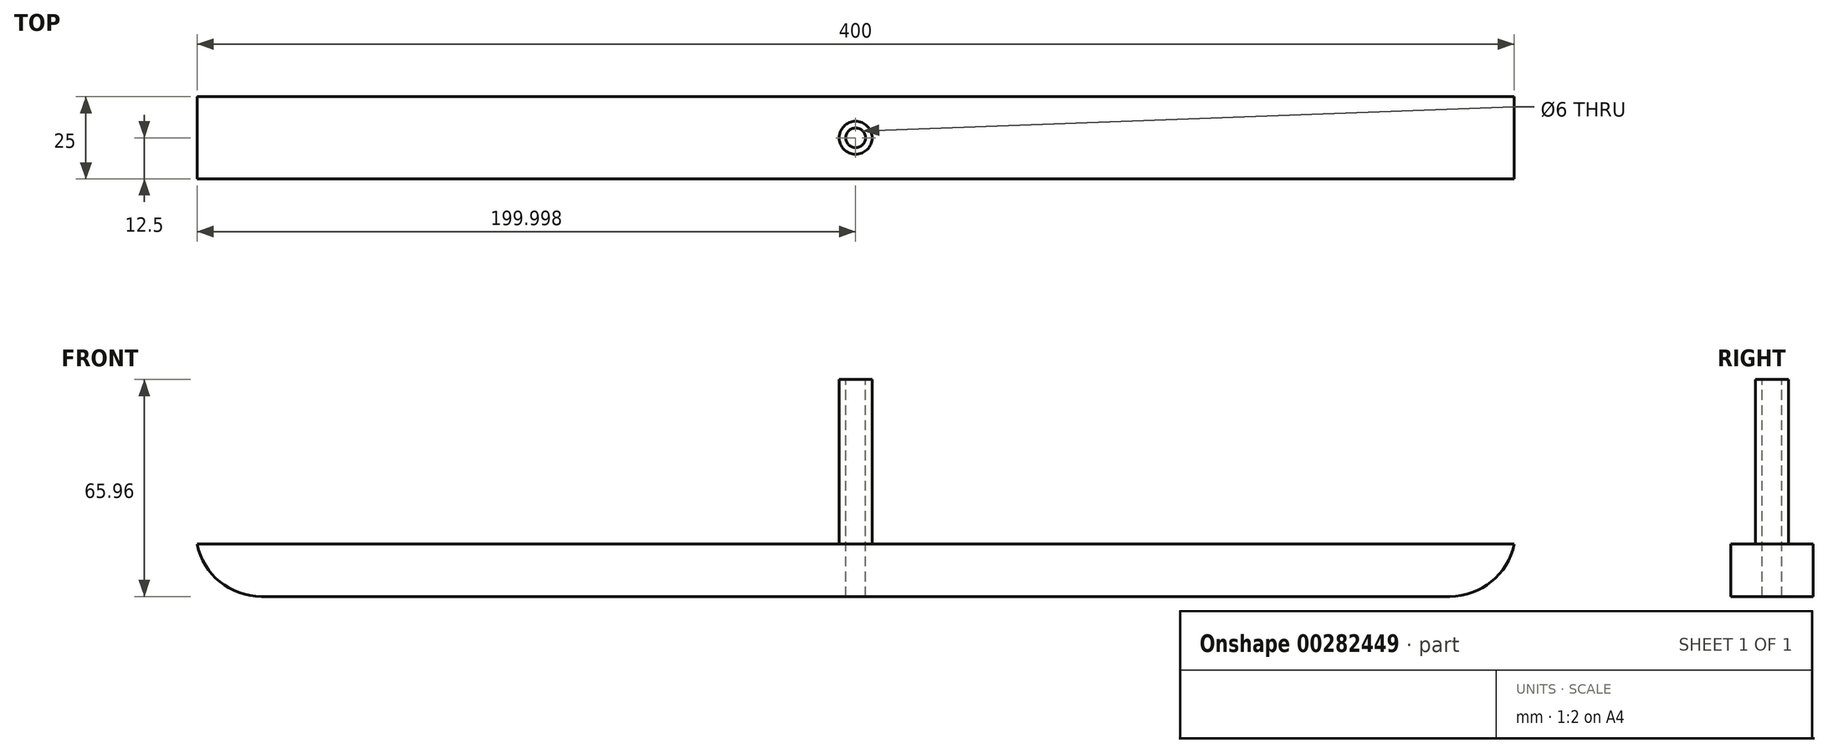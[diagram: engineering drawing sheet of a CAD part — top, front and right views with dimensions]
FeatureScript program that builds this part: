
annotation { "Feature Type Name" : "Feature", "Feature Type Description" : "" }
export const myFeature = defineFeature(function(context is Context, id is Id, definition is map)
    precondition{}
    {
        {
            var Q0;
            Q0=qCreatedBy(makeId("Front.planeOp"),FACE);
            var sketch = newSketch(context, id + "F0", { "sketchPlane" : qUnion([Q0])});
            skLineSegment(sketch, "E0.bottom", {"start": v(-70.22, 41.14) * mm, "end": v(329.78, 41.14) * mm});
            skLineSegment(sketch, "E0.top", {"start": v(-70.22, 25.18) * mm, "end": v(329.78, 25.18) * mm});
            skLineSegment(sketch, "E0.left", {"start": v(-70.22, 41.14) * mm, "end": v(-70.22, 25.18) * mm});
            skLineSegment(sketch, "E0.right", {"start": v(329.78, 41.14) * mm, "end": v(329.78, 25.18) * mm});
            skLineSegment(sketch, "E1.bottom", {"start": v(-70.22, 25.18) * mm, "end": v(-60.22, 25.18) * mm});
            skLineSegment(sketch, "E1.top", {"start": v(-70.22, -49.82) * mm, "end": v(-60.22, -49.82) * mm});
            skLineSegment(sketch, "E1.left", {"start": v(-70.22, 25.18) * mm, "end": v(-70.22, -49.82) * mm});
            skLineSegment(sketch, "E1.right", {"start": v(-60.22, 25.18) * mm, "end": v(-60.22, -49.82) * mm});
            skLineSegment(sketch, "E2.bottom", {"start": v(329.78, 25.18) * mm, "end": v(319.78, 25.18) * mm});
            skLineSegment(sketch, "E2.top", {"start": v(329.78, -49.82) * mm, "end": v(319.78, -49.82) * mm});
            skLineSegment(sketch, "E2.left", {"start": v(329.78, 25.18) * mm, "end": v(329.78, -49.82) * mm});
            skLineSegment(sketch, "E2.right", {"start": v(319.78, 25.18) * mm, "end": v(319.78, -49.82) * mm});
            skLineSegment(sketch, "E3", {"start": v(129.78, 25.18) * mm, "end": v(129.78, 66.56) * mm});
            skPoint(sketch, "E3.endSnap0", {"position": v(129.78, 41.14) * mm});
            skSolve(sketch);
        }
        {
            var Q0;
            Q0=makeQuery(id+"F0.imprint","IMPRINT",FACE,{"disambiguationData":[TD([[makeQuery(id+"F0.imprint","IMPRINT",EDGE,{"derivedFrom":sQuery(id+"F0.wireOp",EDGE,"E0.bottom")}),-1.0]])]});
            var Q1;
            Q1=makeQuery(id+"F0.imprint","IMPRINT",FACE,{"disambiguationData":[TD([[makeQuery(id+"F0.imprint","IMPRINT",EDGE,{"derivedFrom":sQuery(id+"F0.wireOp",EDGE,"E1.bottom")}),-1.0]])]});
            var Q2;
            Q2=makeQuery(id+"F0.imprint","IMPRINT",FACE,{"disambiguationData":[TD([[makeQuery(id+"F0.imprint","IMPRINT",EDGE,{"derivedFrom":sQuery(id+"F0.wireOp",EDGE,"E2.bottom")}),1.0]])]});
            extrude(context, id + "F1", {"entities" : qUnion([Q0, Q1, Q2]), "endBound" : BoundingType.SYMMETRIC, "depth" : 25 * mm});
        }
        {
            var Q0;
            Q0=makeQuery(id+"F1.opExtrude","SWEPT_FACE",FACE,{"disambiguationData":[OSD([sQuery(id+"F0.wireOp",EDGE,"E0.left"),sQuery(id+"F0.wireOp",EDGE,"E1.left")])]});
            var sketch = newSketch(context, id + "F2", { "sketchPlane" : qUnion([Q0])});
            skCircle(sketch, "E4", {"center": v(0, -29.82) * mm, "radius": 5 * mm});
            skSolve(sketch);
        }
        {
            var Q0;
            Q0=makeQuery(id+"F2.imprint","IMPRINT",FACE,{"disambiguationData":[TD([[makeQuery(id+"F2.imprint","IMPRINT",EDGE,{"derivedFrom":sQuery(id+"F2.wireOp",EDGE,"E4")}),1.0]])]});
            extrude(context, id + "F3", {"entities" : qUnion([Q0]), "operationType" : NewBodyOperationType.REMOVE, "endBound" : BoundingType.THROUGH_ALL, "oppositeDirection" : true, "depth" : 25 * mm});
        }
        {
            var Q0;
            Q0=makeQuery(id+"F1.opExtrude","SWEPT_FACE",FACE,{"disambiguationData":[OSD([sQuery(id+"F0.wireOp",EDGE,"E0.bottom")])]});
            var sketch = newSketch(context, id + "F4", { "sketchPlane" : qUnion([Q0])});
            skCircle(sketch, "E5", {"center": v(129.78, 0) * mm, "radius": 5 * mm});
            skSolve(sketch);
        }
        {
            var Q0;
            Q0=makeQuery(id+"F4.imprint","IMPRINT",FACE,{"disambiguationData":[TD([[makeQuery(id+"F4.imprint","IMPRINT",EDGE,{"derivedFrom":sQuery(id+"F4.wireOp",EDGE,"E5")}),1.0]])]});
            extrude(context, id + "F5", {"entities" : qUnion([Q0]), "operationType" : NewBodyOperationType.ADD, "depth" : 50 * mm});
        }
        {
            var Q0;
            Q0=makeQuery(id+"F1.opExtrude","SWEPT_EDGE",EDGE,{"disambiguationData":[OSD([sQuery(id+"F0.wireOp",EDGE,"E0.top"),sQuery(id+"F0.wireOp",EDGE,"E1.bottom"),sQuery(id+"F0.wireOp",EDGE,"E1.right")])]});
            var Q1;
            Q1=makeQuery(id+"F1.opExtrude","SWEPT_EDGE",EDGE,{"disambiguationData":[OSD([sQuery(id+"F0.wireOp",EDGE,"E0.top"),sQuery(id+"F0.wireOp",EDGE,"E2.bottom"),sQuery(id+"F0.wireOp",EDGE,"E2.right")])]});
            fillet(context, id + "F6", {"entities" : qUnion([Q0, Q1]), "radius" : 20 * mm, "tangentPropagation" : true, "allowEdgeOverflow" : false});
        }
        {
            var Q0;
            Q0=makeQuery(id+"F5.opExtrude","CAP_FACE",FACE,{"disambiguationData":[OSD([sQuery(id+"F4.wireOp",EDGE,"E5")])],"isStart":false});
            var sketch = newSketch(context, id + "F7", { "sketchPlane" : qUnion([Q0])});
            skCircle(sketch, "E6", {"center": v(129.78, 0) * mm, "radius": 3 * mm});
            skSolve(sketch);
        }
        {
            var Q0;
            Q0=makeQuery(id+"F7.imprint","IMPRINT",FACE,{"disambiguationData":[TD([[makeQuery(id+"F7.imprint","IMPRINT",EDGE,{"derivedFrom":sQuery(id+"F7.wireOp",EDGE,"E6")}),1.0]])]});
            extrude(context, id + "F8", {"entities" : qUnion([Q0]), "operationType" : NewBodyOperationType.REMOVE, "endBound" : BoundingType.THROUGH_ALL, "oppositeDirection" : true, "depth" : 25 * mm});
        }
    });
